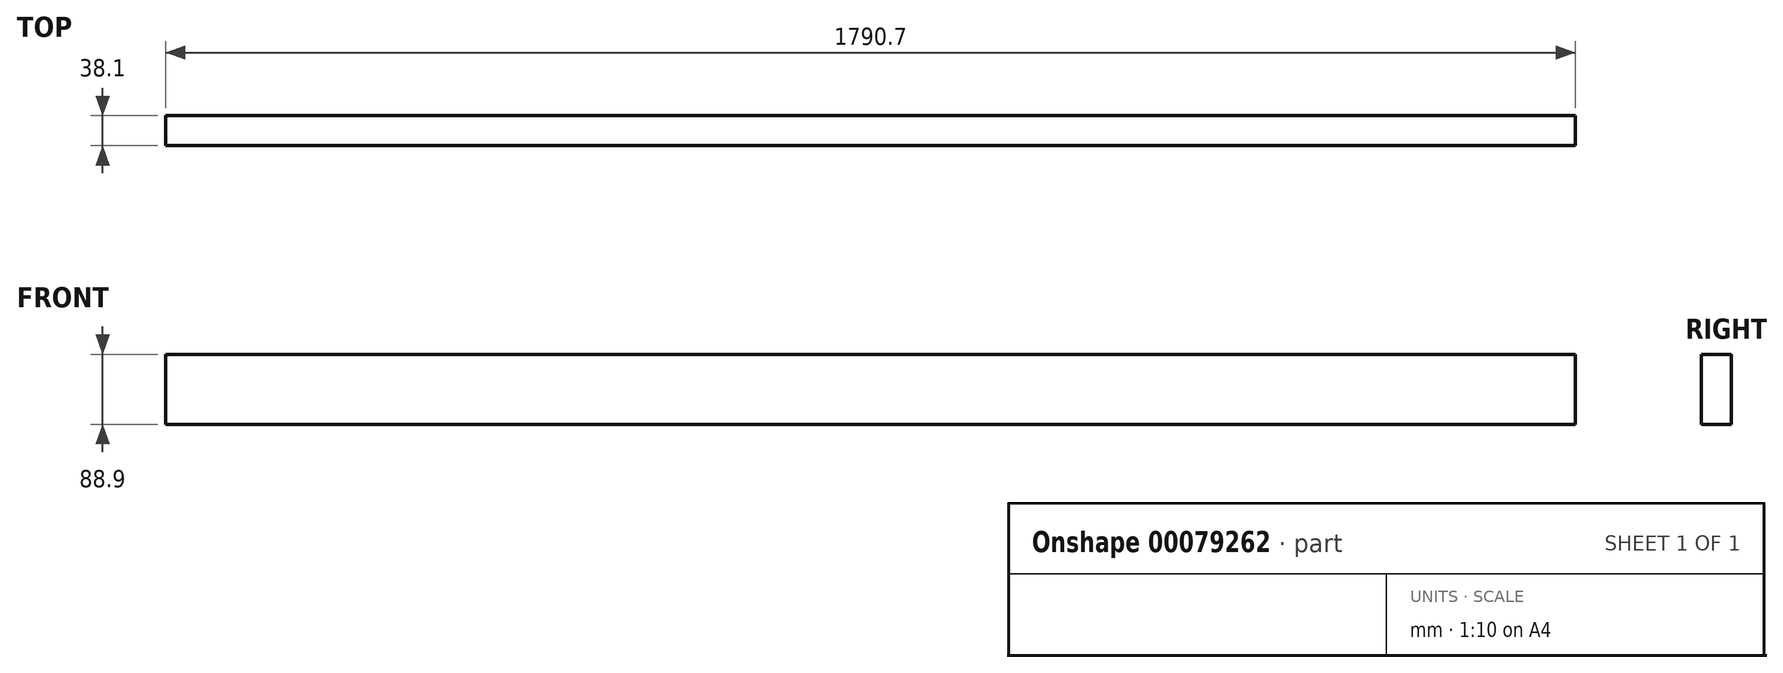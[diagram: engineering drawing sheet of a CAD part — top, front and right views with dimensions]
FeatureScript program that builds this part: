
annotation { "Feature Type Name" : "Feature", "Feature Type Description" : "" }
export const myFeature = defineFeature(function(context is Context, id is Id, definition is map)
    precondition{}
    {
        {
            var Q0;
            Q0=qCreatedBy(makeId("Right.planeOp"),FACE);
            var sketch = newSketch(context, id + "F0", { "sketchPlane" : qUnion([Q0])});
            skLineSegment(sketch, "E0.bottom", {"start": v(0, 0) * mm, "end": v(-38.1, 0) * mm});
            skLineSegment(sketch, "E0.top", {"start": v(0, 88.9) * mm, "end": v(-38.1, 88.9) * mm});
            skLineSegment(sketch, "E0.left", {"start": v(0, 0) * mm, "end": v(0, 88.9) * mm});
            skLineSegment(sketch, "E0.right", {"start": v(-38.1, 0) * mm, "end": v(-38.1, 88.9) * mm});
            skSolve(sketch);
        }
        {
            var Q0;
            Q0=makeQuery(id+"F0.imprint","IMPRINT",FACE,{"disambiguationData":[TD([[makeQuery(id+"F0.imprint","IMPRINT",EDGE,{"derivedFrom":sQuery(id+"F0.wireOp",EDGE,"E0.bottom")}),-1.0]])]});
            extrude(context, id + "F1", {"entities" : qUnion([Q0]), "depth" : 1790.7 * mm});
        }
    });
